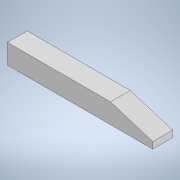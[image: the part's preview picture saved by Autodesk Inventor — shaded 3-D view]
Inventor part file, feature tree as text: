
AUTODESK INVENTOR PART (.ipt)
format: ipt  version: 2021 (Build 250183000, 183)  size: 107,520 bytes
history: native  units: mm
features: sketch x2, other x1, extrude x1, chamfer x1, hole x1
ambient origin geometry x8: Origin, YZ Plane, XZ Plane, XY Plane, X Axis, Y Axis, Z Axis, Center Point
bodies: Body1 (feature_tree)
feature tree (6):
  other  "Sólido1"
  extrude  "Extrusão1"  Depth=15.0mm
  chamfer  "Chanfro1"  Distance=15.0mm
  hole  "Furo1"  [1 undecoded]
  sketch  "Esboço1"  dims[d0=110.0mm d1=15.0mm d2=15.0mm d3=0.0mm]
  sketch  "Esboço2"  dims[d4=10.0mm d5=32.0mm d6=45.0deg d7=7.5mm d8=13.0mm d9=8.0mm d10=6.0mm d11=4.0mm d12=2.0mm d13=90.0deg d14=10.4mm d15=20.594885mm d25=53.0mm]
note: 1 required parameter value undecoded (feature->parameter linkage not recoverable at this tier; creation-order binding heuristic only, values carry confidence <= 0.55)
